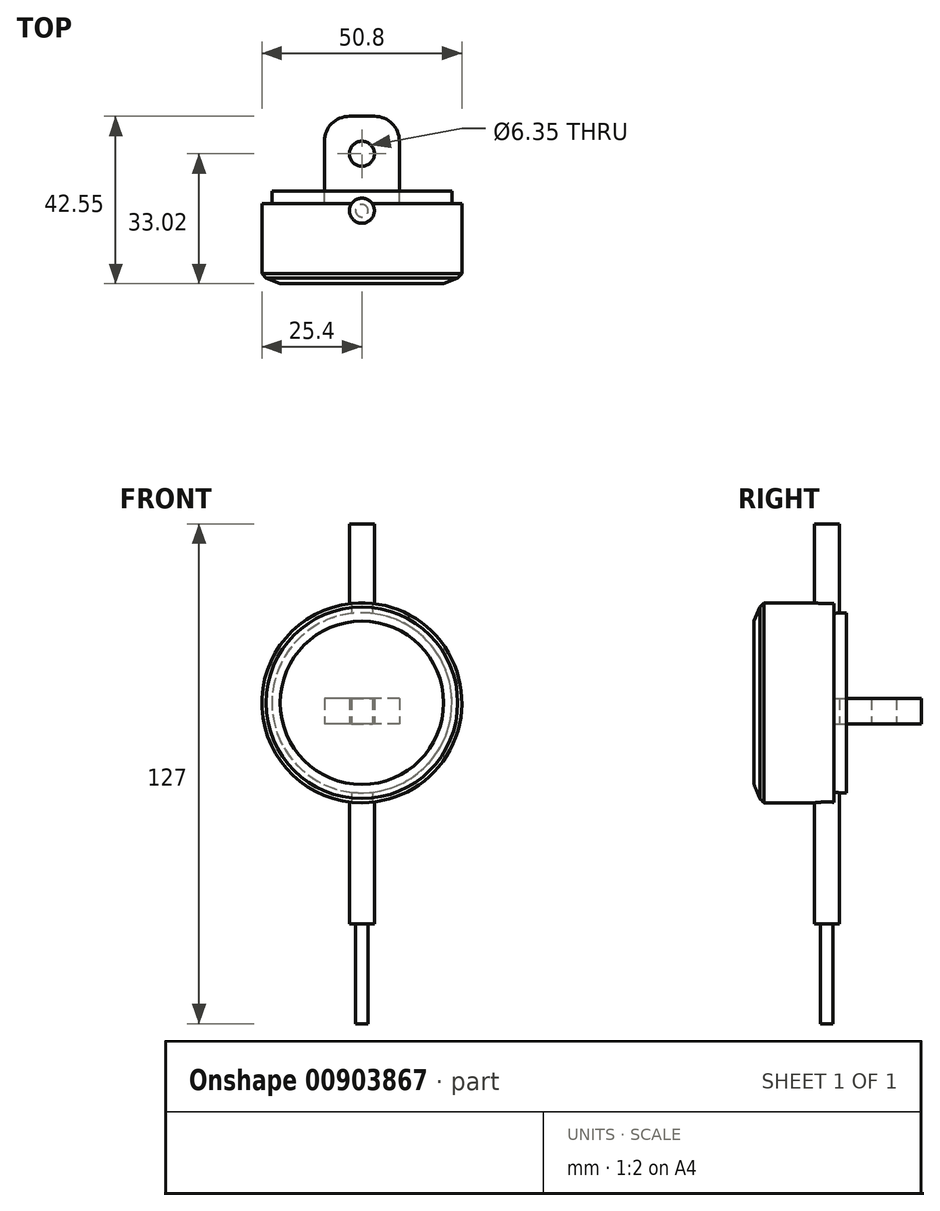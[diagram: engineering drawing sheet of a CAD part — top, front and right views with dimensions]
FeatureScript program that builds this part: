
annotation { "Feature Type Name" : "Feature", "Feature Type Description" : "" }
export const myFeature = defineFeature(function(context is Context, id is Id, definition is map)
    precondition{}
    {
        {
            var Q0;
            Q0=qCreatedBy(makeId("Top.planeOp"),FACE);
            var sketch = newSketch(context, id + "F0", { "sketchPlane" : qUnion([Q0])});
            skLineSegment(sketch, "E0.bottom", {"start": v(3.18, 9.53) * mm, "end": v(-3.18, 9.53) * mm});
            skLineSegment(sketch, "E0.top", {"start": v(9.52, -9.53) * mm, "end": v(-9.53, -9.53) * mm});
            skLineSegment(sketch, "E0.left", {"start": v(9.53, 3.17) * mm, "end": v(9.52, -9.53) * mm});
            skLineSegment(sketch, "E0.right", {"start": v(-9.53, 3.18) * mm, "end": v(-9.53, -9.53) * mm});
            skPoint(sketch, "E0.middle", {"position": v(0, 0) * mm});
            skPoint(sketch, "E1.visualSharp", {"position": v(-9.52, 9.53) * mm});
            skArc(sketch, "E1.filletArc", {"start": v(-3.18, 9.53) * mm, "mid": v(-7.67, 7.67) * mm, "end": v(-9.53, 3.18) * mm});
            skPoint(sketch, "E2.visualSharp", {"position": v(9.53, 9.53) * mm});
            skArc(sketch, "E2.filletArc", {"start": v(9.52, 3.17) * mm, "mid": v(7.67, 7.67) * mm, "end": v(3.17, 9.52) * mm});
            skCircle(sketch, "E3", {"center": v(0, 0) * mm, "radius": 3.18 * mm});
            skSolve(sketch);
        }
        {
            var Q0;
            Q0=makeQuery(id+"F0.imprint","IMPRINT",FACE,{"disambiguationData":[TD([[makeQuery(id+"F0.imprint","IMPRINT",EDGE,{"derivedFrom":sQuery(id+"F0.wireOp",EDGE,"E0.bottom")}),1.0]])]});
            extrude(context, id + "F1", {"entities" : qUnion([Q0]), "depth" : 6.48 * mm, "offsetDistance" : 25.4 * mm});
        }
        {
            var Q0;
            Q0=makeQuery(id+"F1.opExtrude","SWEPT_FACE",FACE,{"disambiguationData":[OSD([sQuery(id+"F0.wireOp",EDGE,"E0.top")])]});
            var sketch = newSketch(context, id + "F2", { "sketchPlane" : qUnion([Q0])});
            skCircle(sketch, "E4", {"center": v(0, 5.32) * mm, "radius": 22.86 * mm});
            skSolve(sketch);
        }
        {
            var Q0;
            Q0=makeQuery(id+"F2.imprint","IMPRINT",FACE,{"disambiguationData":[TD([[makeQuery(id+"F2.imprint","IMPRINT",EDGE,{"derivedFrom":sQuery(id+"F2.wireOp",EDGE,"E4")}),1.0]])]});
            extrude(context, id + "F3", {"entities" : qUnion([Q0]), "depth" : 3.17 * mm, "offsetDistance" : 25.4 * mm});
        }
        {
            var Q0;
            Q0=makeQuery(id+"F3.opExtrude","CAP_FACE",FACE,{"disambiguationData":[OSD([sQuery(id+"F0.wireOp",EDGE,"E0.top"),sQuery(id+"F0.wireOp",EDGE,"E0.left"),sQuery(id+"F0.wireOp",EDGE,"E0.right"),sQuery(id+"F2.wireOp",EDGE,"E4")])],"isStart":false});
            var sketch = newSketch(context, id + "F4", { "sketchPlane" : qUnion([Q0])});
            skCircle(sketch, "E5", {"center": v(0, 5.32) * mm, "radius": 25.4 * mm});
            skSolve(sketch);
        }
        {
            var Q0;
            Q0=makeQuery(id+"F4.imprint","IMPRINT",FACE,{"disambiguationData":[TD([[makeQuery(id+"F4.imprint","IMPRINT",EDGE,{"derivedFrom":sQuery(id+"F4.wireOp",EDGE,"E5")}),1.0]])]});
            var Q1;
            {var subQ0=sQuery(id+"F0.wireOp",EDGE,"E0.top");Q1=makeQuery(id+"F4.imprint","IMPRINT",FACE,{"disambiguationData":[TD([[makeQuery(id+"F4.imprint","IMPRINT",EDGE,{"derivedFrom":makeQuery(id+"F3.opExtrude","CAP_EDGE",EDGE,{"disambiguationData":[OSD([subQ0]),TDD([makeQuery(id+"F2.imprint","IMPRINT",EDGE,{"derivedFrom":makeQuery(id+"F1.opExtrude","CAP_EDGE",EDGE,{"disambiguationData":[OSD([subQ0])],"isStart":true})})])],"isStart":false})}),-1.0]])]});}
            var Q2;
            Q2=makeQuery(id+"F4.imprint","IMPRINT",FACE,{"disambiguationData":[TD([[makeQuery(id+"F4.imprint","IMPRINT",EDGE,{"derivedFrom":makeQuery(id+"F3.opExtrude","CAP_EDGE",EDGE,{"disambiguationData":[OSD([sQuery(id+"F2.wireOp",EDGE,"E4")])],"isStart":false})}),1.0]])]});
            extrude(context, id + "F5", {"entities" : qUnion([Q0, Q1, Q2]), "operationType" : NewBodyOperationType.ADD, "depth" : 20.32 * mm, "offsetDistance" : 25.4 * mm});
        }
        {
            var Q0;
            Q0=makeQuery(id+"F5.opExtrude","CAP_FACE",FACE,{"disambiguationData":[OSD([sQuery(id+"F4.wireOp",EDGE,"E5")])],"isStart":false});
            chamfer(context, id + "F6", {"entities" : qUnion([Q0]), "width" : 2.54 * mm, "tangentPropagation" : true});
        }
        {
            var Q0;
            {var subQ0=sQuery(id+"F4.wireOp",EDGE,"E5");Q0=makeQuery(id+"F6.opChamfer","BLEND_EDGE",EDGE,{"blendedFrom":[makeQuery(id+"F5.opExtrude","CAP_EDGE",EDGE,{"disambiguationData":[OSD([subQ0])],"isStart":false}),makeQuery(id+"F5.opExtrude","CAP_FACE",FACE,{"disambiguationData":[OSD([subQ0])],"isStart":false})],"blendedInto":[makeQuery(id+"F5.opExtrude","CAP_FACE",FACE,{"disambiguationData":[OSD([subQ0])],"isStart":false})]});}
            chamfer(context, id + "F7", {"entities" : qUnion([Q0]), "width" : 5.08 * mm, "tangentPropagation" : true});
        }
        {
            var Q0;
            Q0=qCreatedBy(makeId("Top.planeOp"),FACE);
            var sketch = newSketch(context, id + "F8", { "sketchPlane" : qUnion([Q0])});
            skCircle(sketch, "E6", {"center": v(0, -14.47) * mm, "radius": 3.18 * mm});
            skSolve(sketch);
        }
        {
            var Q0;
            Q0 = qSketchRegion(id + "F8", true);
            extrude(context, id + "F9", {"entities" : qUnion([Q0]), "operationType" : NewBodyOperationType.ADD, "depth" : 50.8 * mm, "offsetDistance" : 25.4 * mm, "hasSecondDirection" : true, "secondDirectionOppositeDirection" : true, "secondDirectionDepth" : 50.8 * mm});
        }
        {
            var Q0;
            Q0=makeQuery(id+"F9.opExtrude","CAP_FACE",FACE,{"disambiguationData":[OSD([sQuery(id+"F8.wireOp",EDGE,"E6")])],"isStart":true});
            var sketch = newSketch(context, id + "F10", { "sketchPlane" : qUnion([Q0])});
            skCircle(sketch, "E7", {"center": v(0, 14.47) * mm, "radius": 1.59 * mm});
            skSolve(sketch);
        }
        {
            var Q0;
            Q0 = qSketchRegion(id + "F10", true);
            extrude(context, id + "F11", {"entities" : qUnion([Q0]), "operationType" : NewBodyOperationType.ADD, "depth" : 25.4 * mm, "offsetDistance" : 25.4 * mm});
        }
    });
